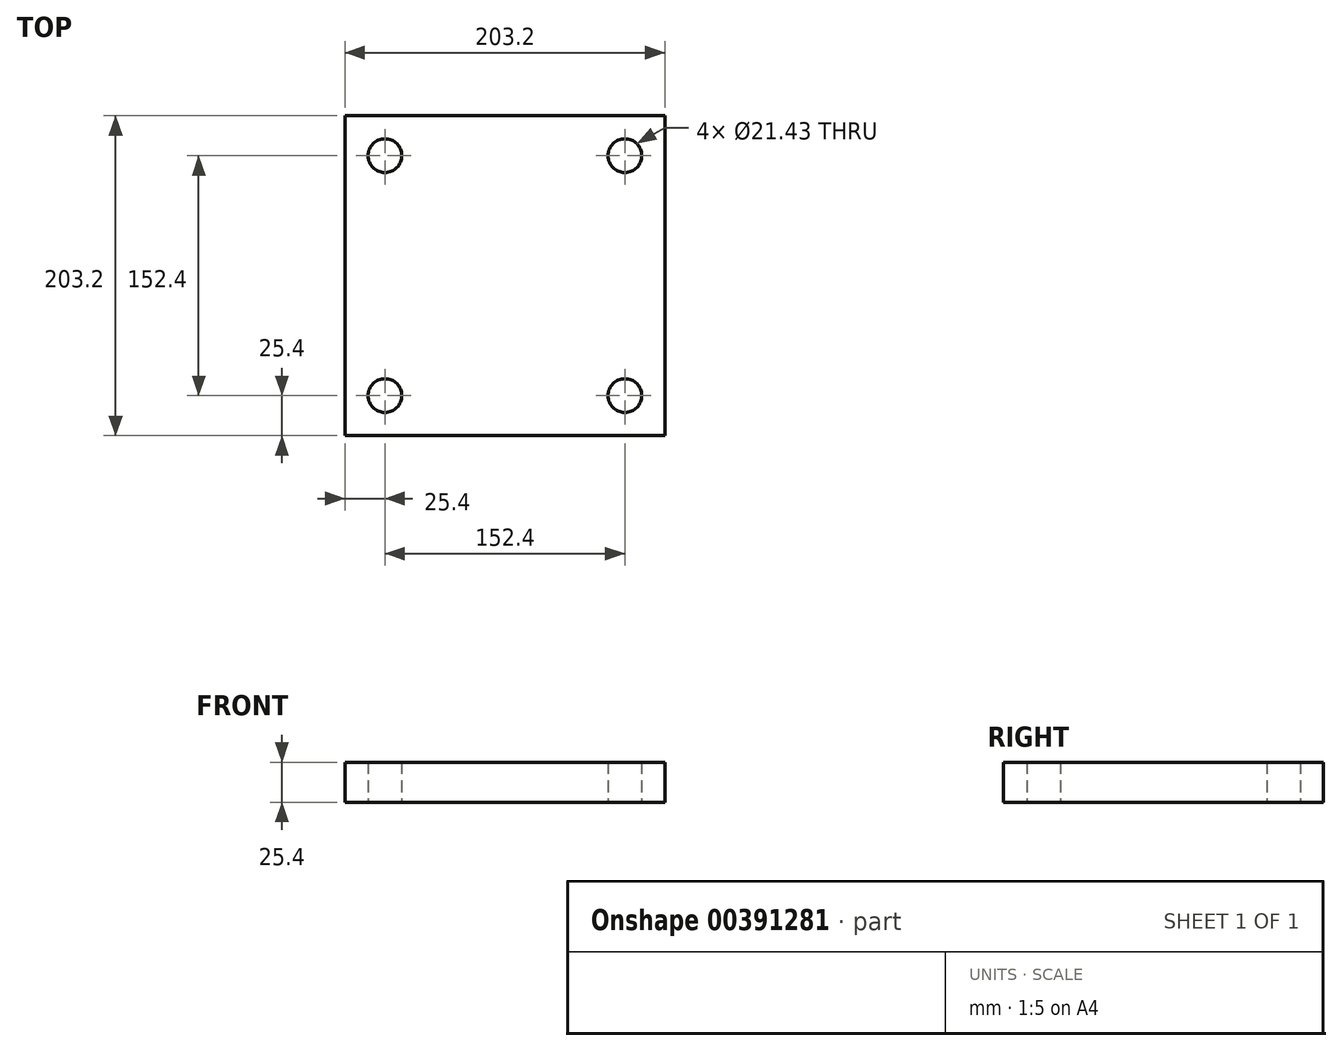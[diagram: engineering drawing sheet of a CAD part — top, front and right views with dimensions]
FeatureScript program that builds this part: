
annotation { "Feature Type Name" : "Feature", "Feature Type Description" : "" }
export const myFeature = defineFeature(function(context is Context, id is Id, definition is map)
    precondition{}
    {
        {
            var Q0;
            Q0=qCreatedBy(makeId("Top.planeOp"),FACE);
            var sketch = newSketch(context, id + "F0", { "sketchPlane" : qUnion([Q0])});
            skLineSegment(sketch, "E0.bottom", {"start": v(-101.6, 101.6) * mm, "end": v(101.6, 101.6) * mm});
            skLineSegment(sketch, "E0.top", {"start": v(-101.6, -101.6) * mm, "end": v(101.6, -101.6) * mm});
            skLineSegment(sketch, "E0.left", {"start": v(-101.6, 101.6) * mm, "end": v(-101.6, -101.6) * mm});
            skLineSegment(sketch, "E0.right", {"start": v(101.6, 101.6) * mm, "end": v(101.6, -101.6) * mm});
            skPoint(sketch, "E0.middle", {"position": v(0, 0) * mm});
            skCircle(sketch, "E1", {"center": v(-76.2, 76.2) * mm, "radius": 10.72 * mm});
            skCircle(sketch, "E2.MirrorC", {"center": v(76.2, 76.2) * mm, "radius": 10.72 * mm});
            skCircle(sketch, "E3.MirrorC", {"center": v(76.2, -76.2) * mm, "radius": 10.72 * mm});
            skCircle(sketch, "E4.MirrorC", {"center": v(-76.2, -76.2) * mm, "radius": 10.72 * mm});
            skSolve(sketch);
        }
        {
            var Q0;
            Q0=makeQuery(id+"F0.imprint","IMPRINT",FACE,{"disambiguationData":[TD([[makeQuery(id+"F0.imprint","IMPRINT",EDGE,{"derivedFrom":sQuery(id+"F0.wireOp",EDGE,"E0.bottom")}),-1.0]])]});
            extrude(context, id + "F1", {"entities" : qUnion([Q0]), "depth" : 25.4 * mm});
        }
    });
